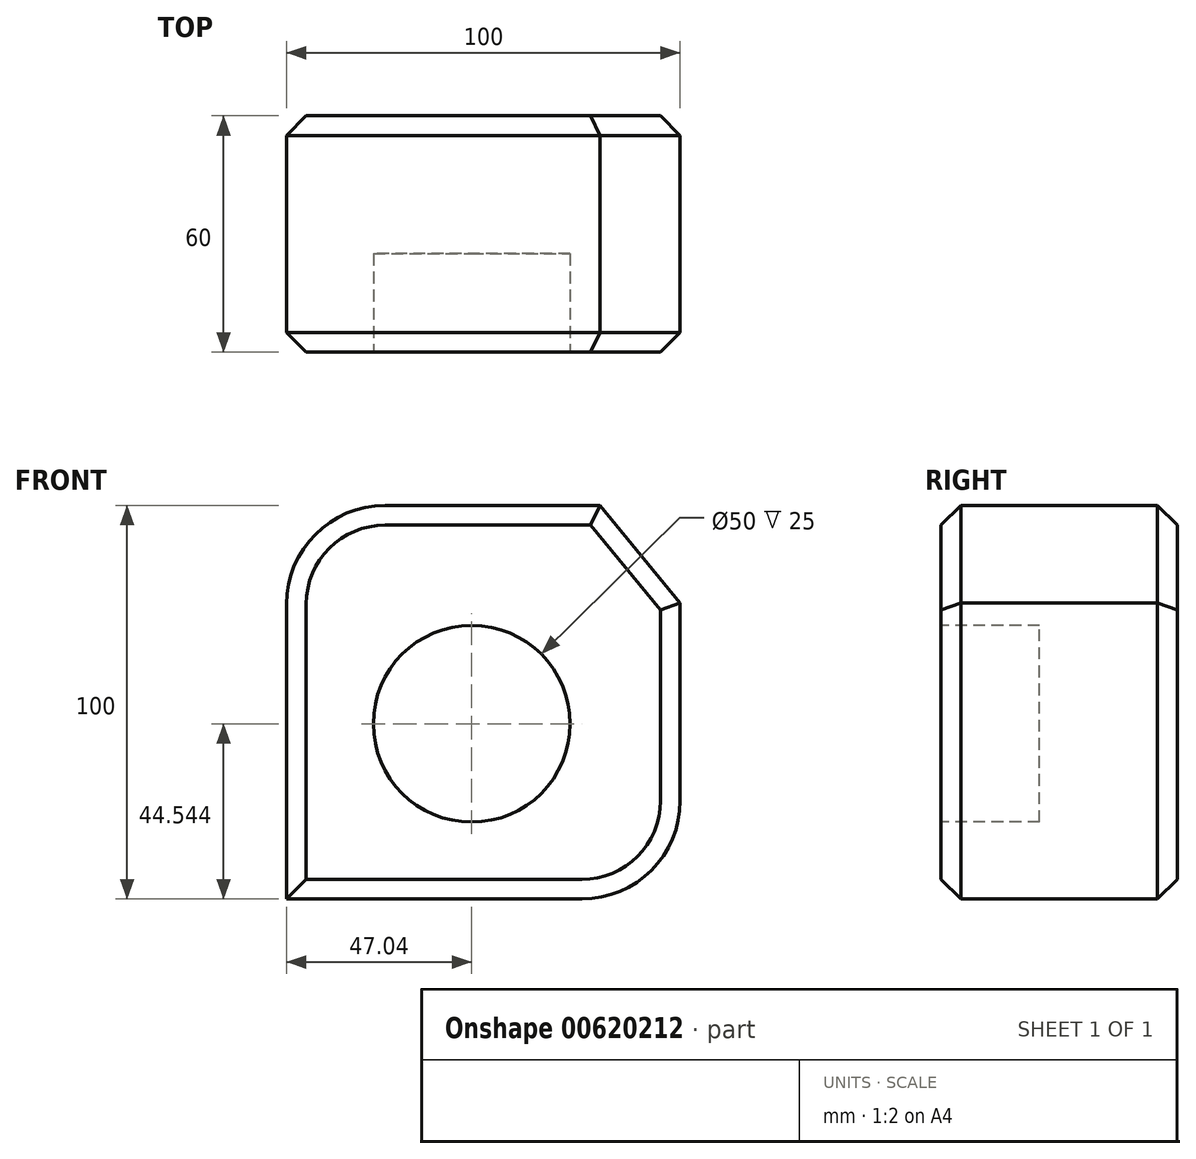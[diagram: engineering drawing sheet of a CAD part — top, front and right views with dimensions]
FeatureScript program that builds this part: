
annotation { "Feature Type Name" : "Feature", "Feature Type Description" : "" }
export const myFeature = defineFeature(function(context is Context, id is Id, definition is map)
    precondition{}
    {
        {
            var Q0;
            Q0=qCreatedBy(makeId("Front.planeOp"),FACE);
            var sketch = newSketch(context, id + "F0", { "sketchPlane" : qUnion([Q0])});
            skLineSegment(sketch, "E0.bottom", {"start": v(-22.04, 24.76) * mm, "end": v(32.58, 24.76) * mm});
            skLineSegment(sketch, "E0.top", {"start": v(-47.04, -75.24) * mm, "end": v(27.96, -75.24) * mm});
            skLineSegment(sketch, "E0.left", {"start": v(-47.04, -0.24) * mm, "end": v(-47.04, -75.24) * mm});
            skLineSegment(sketch, "E0.right", {"start": v(52.96, 0) * mm, "end": v(52.96, -50.24) * mm});
            skPoint(sketch, "E1.visualSharp", {"position": v(52.96, -75.24) * mm});
            skArc(sketch, "E1.filletArc", {"start": v(27.96, -75.24) * mm, "mid": v(45.64, -67.92) * mm, "end": v(52.96, -50.24) * mm});
            skPoint(sketch, "E2.visualSharp", {"position": v(-47.04, 24.76) * mm});
            skArc(sketch, "E2.filletArc", {"start": v(-22.04, 24.76) * mm, "mid": v(-39.71, 17.44) * mm, "end": v(-47.04, -0.24) * mm});
            skLineSegment(sketch, "E3", {"start": v(34.51, 22.42) * mm, "end": v(52.96, 0) * mm});
            skPoint(sketch, "E3.endSnap0", {"position": v(52.96, 18.01) * mm});
            skLineSegment(sketch, "E4", {"start": v(34.51, 22.42) * mm, "end": v(32.58, 24.76) * mm});
            skPoint(sketch, "E5.orphan", {"position": v(52.96, 24.76) * mm});
            skPoint(sketch, "E6.orphan", {"position": v(52.96, 11.27) * mm});
            skSolve(sketch);
        }
        {
            var Q0;
            Q0 = qSketchRegion(id + "F0", true);
            extrude(context, id + "F1", {"entities" : qUnion([Q0]), "depth" : 60 * mm, "offsetDistance" : 25 * mm});
        }
        {
            var Q0;
            Q0=makeQuery(id+"F1.opExtrude","CAP_EDGE",EDGE,{"disambiguationData":[OSD([sQuery(id+"F0.wireOp",EDGE,"E2.filletArc")])],"isStart":false});
            var Q1;
            Q1=makeQuery(id+"F1.opExtrude","CAP_EDGE",EDGE,{"disambiguationData":[OSD([sQuery(id+"F0.wireOp",EDGE,"E0.bottom")])],"isStart":false});
            var Q2;
            Q2=makeQuery(id+"F1.opExtrude","CAP_EDGE",EDGE,{"disambiguationData":[OSD([sQuery(id+"F0.wireOp",EDGE,"E3"),sQuery(id+"F0.wireOp",EDGE,"E4")])],"isStart":false});
            var Q3;
            Q3=makeQuery(id+"F1.opExtrude","CAP_EDGE",EDGE,{"disambiguationData":[OSD([sQuery(id+"F0.wireOp",EDGE,"E0.right")])],"isStart":false});
            var Q4;
            Q4=makeQuery(id+"F1.opExtrude","CAP_EDGE",EDGE,{"disambiguationData":[OSD([sQuery(id+"F0.wireOp",EDGE,"E1.filletArc")])],"isStart":false});
            var Q5;
            Q5=makeQuery(id+"F1.opExtrude","CAP_EDGE",EDGE,{"disambiguationData":[OSD([sQuery(id+"F0.wireOp",EDGE,"E0.top")])],"isStart":false});
            var Q6;
            Q6=makeQuery(id+"F1.opExtrude","CAP_EDGE",EDGE,{"disambiguationData":[OSD([sQuery(id+"F0.wireOp",EDGE,"E0.left")])],"isStart":false});
            var Q7;
            Q7=makeQuery(id+"F1.opExtrude","CAP_EDGE",EDGE,{"disambiguationData":[OSD([sQuery(id+"F0.wireOp",EDGE,"E2.filletArc")])],"isStart":true});
            var Q8;
            Q8=makeQuery(id+"F1.opExtrude","CAP_EDGE",EDGE,{"disambiguationData":[OSD([sQuery(id+"F0.wireOp",EDGE,"E0.bottom")])],"isStart":true});
            var Q9;
            Q9=makeQuery(id+"F1.opExtrude","CAP_EDGE",EDGE,{"disambiguationData":[OSD([sQuery(id+"F0.wireOp",EDGE,"E3"),sQuery(id+"F0.wireOp",EDGE,"E4")])],"isStart":true});
            var Q10;
            Q10=makeQuery(id+"F1.opExtrude","CAP_EDGE",EDGE,{"disambiguationData":[OSD([sQuery(id+"F0.wireOp",EDGE,"E1.filletArc")])],"isStart":true});
            var Q11;
            Q11=makeQuery(id+"F1.opExtrude","CAP_EDGE",EDGE,{"disambiguationData":[OSD([sQuery(id+"F0.wireOp",EDGE,"E0.top")])],"isStart":true});
            chamfer(context, id + "F2", {"entities" : qUnion([Q0, Q1, Q2, Q3, Q4, Q5, Q6, Q7, Q8, Q9, Q10, Q11]), "width" : 5 * mm, "tangentPropagation" : true});
        }
        {
            var Q0;
            Q0=makeQuery(id+"F1.opExtrude","CAP_FACE",FACE,{"disambiguationData":[OSD([sQuery(id+"F0.wireOp",EDGE,"E0.bottom"),sQuery(id+"F0.wireOp",EDGE,"E0.top"),sQuery(id+"F0.wireOp",EDGE,"E0.left"),sQuery(id+"F0.wireOp",EDGE,"E0.right"),sQuery(id+"F0.wireOp",EDGE,"E1.filletArc"),sQuery(id+"F0.wireOp",EDGE,"E2.filletArc"),sQuery(id+"F0.wireOp",EDGE,"E3"),sQuery(id+"F0.wireOp",EDGE,"E4")])],"isStart":false});
            var sketch = newSketch(context, id + "F3", { "sketchPlane" : qUnion([Q0])});
            skCircle(sketch, "E7", {"center": v(0, -30.7) * mm, "radius": 25 * mm});
            skSolve(sketch);
        }
        {
            var Q0;
            Q0=makeQuery(id+"F3.imprint","IMPRINT",FACE,{"disambiguationData":[TD([[makeQuery(id+"F3.imprint","IMPRINT",EDGE,{"derivedFrom":sQuery(id+"F3.wireOp",EDGE,"E7")}),1.0]])]});
            extrude(context, id + "F4", {"entities" : qUnion([Q0]), "operationType" : NewBodyOperationType.REMOVE, "oppositeDirection" : true, "depth" : 25 * mm, "offsetDistance" : 25 * mm});
        }
    });
